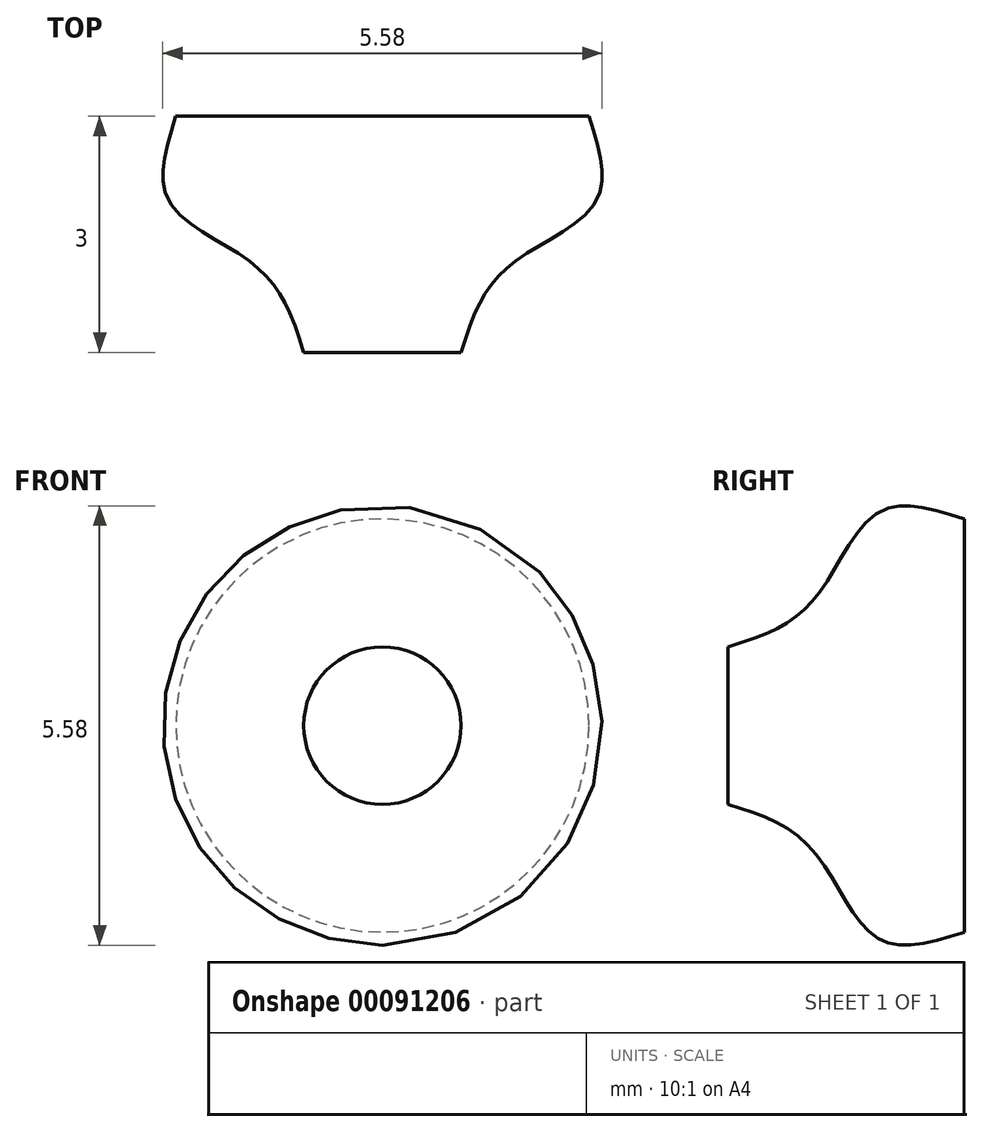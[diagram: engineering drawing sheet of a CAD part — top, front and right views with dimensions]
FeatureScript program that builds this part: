
annotation { "Feature Type Name" : "Feature", "Feature Type Description" : "" }
export const myFeature = defineFeature(function(context is Context, id is Id, definition is map)
    precondition{}
    {
        {
            var Q0;
            Q0=qCreatedBy(makeId("Front.planeOp"),FACE);
            var sketch = newSketch(context, id + "F0", { "sketchPlane" : qUnion([Q0])});
            skCircle(sketch, "E0", {"center": v(0, 0) * mm, "radius": 2.62 * mm});
            skSolve(sketch);
        }
        {
            var Q0;
            Q0=qCreatedBy(makeId("Front.planeOp"),FACE);
            cPlane(context, id + "F1", {"entities" : qUnion([Q0]), "cplaneType" : CPlaneType.OFFSET, "offset" : 1 * mm, "width" : 150 * mm, "height" : 150 * mm});
        }
        {
            var Q0;
            Q0=qCreatedBy(id+"F1.planeOp",FACE);
            var sketch = newSketch(context, id + "F2", { "sketchPlane" : qUnion([Q0])});
            skCircle(sketch, "E1", {"center": v(0, 0) * mm, "radius": 2.75 * mm});
            skSolve(sketch);
        }
        {
            var Q0;
            Q0=qCreatedBy(id+"F1.planeOp",FACE);
            cPlane(context, id + "F3", {"entities" : qUnion([Q0]), "cplaneType" : CPlaneType.OFFSET, "offset" : 1 * mm, "width" : 150 * mm, "height" : 150 * mm});
        }
        {
            var Q0;
            Q0=qCreatedBy(id+"F3.planeOp",FACE);
            var sketch = newSketch(context, id + "F4", { "sketchPlane" : qUnion([Q0])});
            skCircle(sketch, "E2", {"center": v(0, 0) * mm, "radius": 1.5 * mm});
            skSolve(sketch);
        }
        {
            var Q0;
            Q0=qCreatedBy(id+"F3.planeOp",FACE);
            cPlane(context, id + "F5", {"entities" : qUnion([Q0]), "cplaneType" : CPlaneType.OFFSET, "offset" : 1 * mm, "width" : 150 * mm, "height" : 150 * mm});
        }
        {
            var Q0;
            Q0=qCreatedBy(id+"F5.planeOp",FACE);
            var sketch = newSketch(context, id + "F6", { "sketchPlane" : qUnion([Q0])});
            skCircle(sketch, "E3", {"center": v(0, 0) * mm, "radius": 1 * mm});
            skSolve(sketch);
        }
        {
            var Q0;
            Q0 = qSketchRegion(id + "F0", true);
            var Q1;
            Q1 = qSketchRegion(id + "F2", true);
            var Q2;
            Q2 = qSketchRegion(id + "F4", true);
            var Q3;
            Q3 = qSketchRegion(id + "F6", true);
            loft(context, id + "F7", {"sheetProfilesArray" : [{ "sheetProfileEntities" : qUnion([Q0]) }, { "sheetProfileEntities" : qUnion([Q1]) }, { "sheetProfileEntities" : qUnion([Q2]) }, { "sheetProfileEntities" : qUnion([Q3]) }]});
        }
    });
